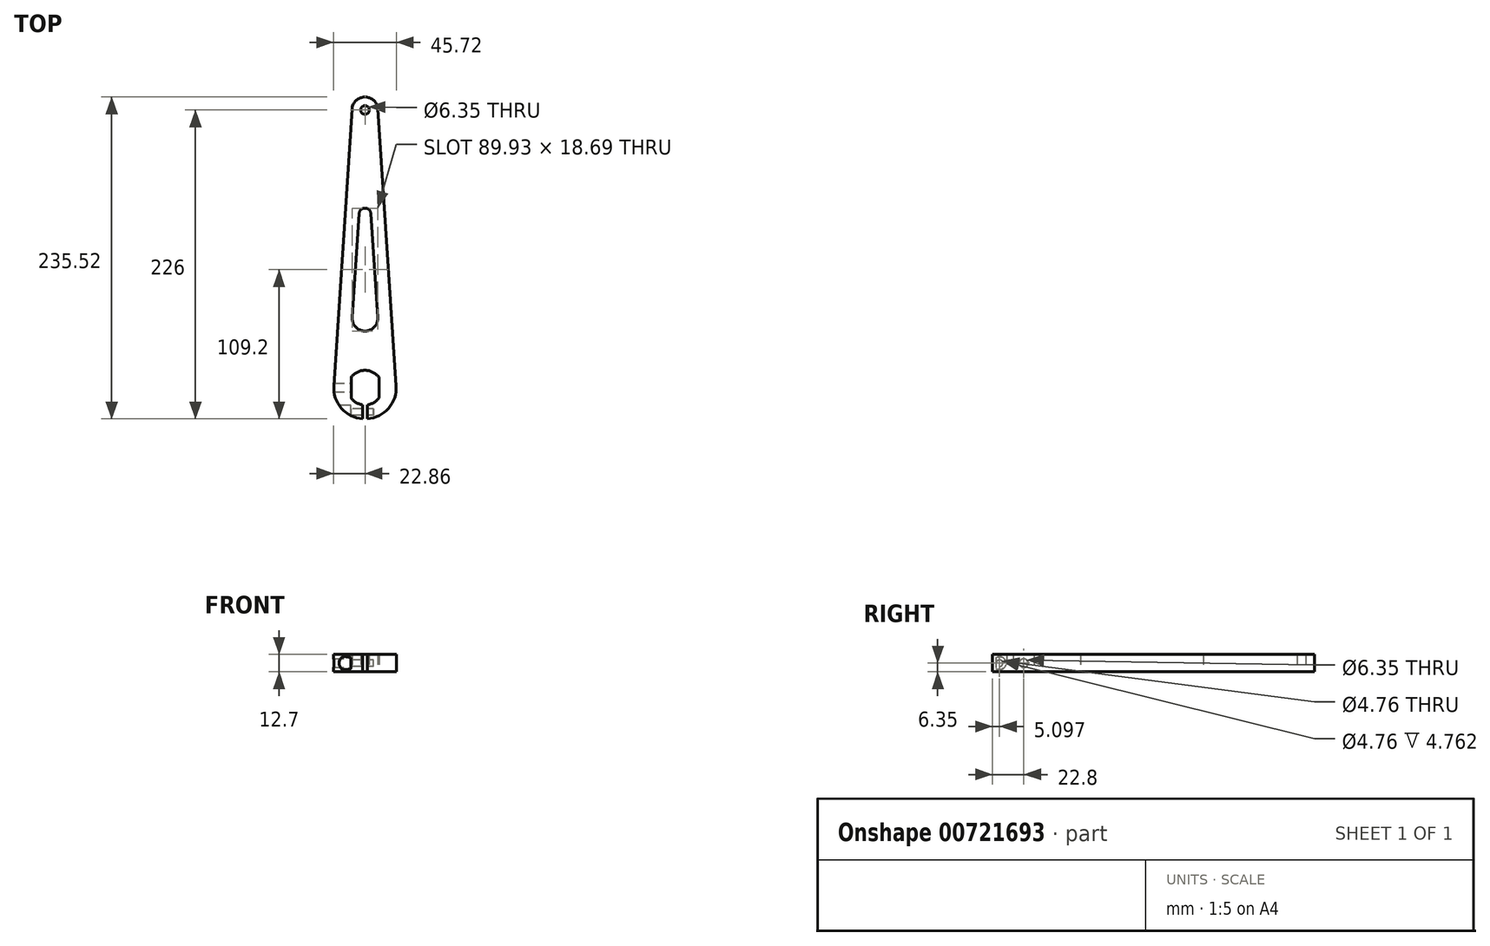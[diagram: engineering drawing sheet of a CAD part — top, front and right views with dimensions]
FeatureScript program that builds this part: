
annotation { "Feature Type Name" : "Feature", "Feature Type Description" : "" }
export const myFeature = defineFeature(function(context is Context, id is Id, definition is map)
    precondition{}
    {
        {
            var Q0;
            Q0=qCreatedBy(makeId("Top.planeOp"),FACE);
            var sketch = newSketch(context, id + "F0", { "sketchPlane" : qUnion([Q0])});
            skLineSegment(sketch, "E0", {"start": v(0, 220.9) * mm, "end": v(0, -303.4) * mm, "construction": true});
            skLineSegment(sketch, "E1", {"start": v(-22.81, 1.5) * mm, "end": v(-9.5, 203.83) * mm});
            skCircle(sketch, "E2", {"center": v(0, 203.2) * mm, "radius": 3.18 * mm});
            skArc(sketch, "E3.0", {"start": v(9.5, 203.83) * mm, "mid": v(0, 212.73) * mm, "end": v(-9.5, 203.83) * mm});
            skArc(sketch, "E4.0", {"start": v(-22.81, 1.5) * mm, "mid": v(-17.22, -15.04) * mm, "end": v(-1.59, -22.8) * mm});
            skLineSegment(sketch, "E5.MirrorCS", {"start": v(22.81, 1.5) * mm, "end": v(9.5, 203.83) * mm});
            skArc(sketch, "E6", {"start": v(-9.35, 51.41) * mm, "mid": v(0, 41.43) * mm, "end": v(9.35, 51.41) * mm});
            skLineSegment(sketch, "E7", {"start": v(9.35, 51.41) * mm, "end": v(4.36, 127.29) * mm});
            skArc(sketch, "E8", {"start": v(4.36, 127.29) * mm, "mid": v(0, 131.37) * mm, "end": v(-4.36, 127.29) * mm});
            skLineSegment(sketch, "E9.MirrorCS", {"start": v(-9.35, 51.41) * mm, "end": v(-4.36, 127.29) * mm});
            skArc(sketch, "E10", {"start": v(10.16, 7.62) * mm, "mid": v(0, 12.7) * mm, "end": v(-10.16, 7.62) * mm});
            skLineSegment(sketch, "E11", {"start": v(-10.16, 7.62) * mm, "end": v(-10.16, -7.62) * mm});
            skLineSegment(sketch, "E12.MirrorCS", {"start": v(10.16, 7.62) * mm, "end": v(10.16, -7.62) * mm});
            skArc(sketch, "E13.trimOffspring", {"start": v(-10.16, -7.62) * mm, "mid": v(-6.38, -10.98) * mm, "end": v(-1.59, -12.6) * mm});
            skLineSegment(sketch, "E14", {"start": v(-1.59, -12.6) * mm, "end": v(-1.59, -22.8) * mm});
            skLineSegment(sketch, "E15.MirrorCS", {"start": v(1.59, -12.6) * mm, "end": v(1.59, -22.8) * mm});
            skArc(sketch, "E16.trimOffspring", {"start": v(1.59, -12.6) * mm, "mid": v(6.38, -10.98) * mm, "end": v(10.16, -7.62) * mm});
            skArc(sketch, "E17.trimOffspring", {"start": v(1.59, -22.8) * mm, "mid": v(17.22, -15.04) * mm, "end": v(22.81, 1.5) * mm});
            skSolve(sketch);
        }
        {
            var Q0;
            Q0=qSketchRegion(id+"F0",true);
            extrude(context, id + "F1", {"entities" : qUnion([Q0]), "depth" : 12.7 * mm, "offsetDistance" : 25.4 * mm});
        }
        {
            var Q0;
            Q0=makeQuery(id+"F1.opExtrude","SWEPT_FACE",FACE,{"disambiguationData":[OSD([sQuery(id+"F0.wireOp",EDGE,"E11")])]});
            var sketch = newSketch(context, id + "F2", { "sketchPlane" : qUnion([Q0])});
            skCircle(sketch, "E18", {"center": v(0, 6.35) * mm, "radius": 3.18 * mm});
            skLineSegment(sketch, "E19", {"start": v(0, 0) * mm, "end": v(0, 12.7) * mm, "construction": true});
            skSolve(sketch);
        }
        {
            var Q0;
            Q0=qSketchRegion(id+"F2",true);
            extrude(context, id + "F3", {"entities" : qUnion([Q0]), "operationType" : NewBodyOperationType.REMOVE, "oppositeDirection" : true, "depth" : 25.4 * mm, "offsetDistance" : 25.4 * mm});
        }
        {
            var Q0;
            Q0=qCreatedBy(makeId("Right.planeOp"),FACE);
            var sketch = newSketch(context, id + "F4", { "sketchPlane" : qUnion([Q0])});
            skLineSegment(sketch, "E20", {"start": v(-22.8, 12.7) * mm, "end": v(-12.6, 12.7) * mm, "construction": true});
            skLineSegment(sketch, "E21", {"start": v(-17.7, 12.7) * mm, "end": v(-17.7, 0) * mm, "construction": true});
            skCircle(sketch, "E22", {"center": v(-17.7, 6.35) * mm, "radius": 2.38 * mm});
            skSolve(sketch);
        }
        {
            var Q0;
            Q0=qSketchRegion(id+"F4",true);
            var Q1;
            Q1=qConstructionFilter(qBodyType(qCreatedBy(id+"F4",EDGE),BodyType.WIRE),ConstructionObject.NO);
            extrude(context, id + "F5", {"entities" : qUnion([Q0]), "operationType" : NewBodyOperationType.REMOVE, "surfaceEntities" : qUnion([Q1]), "depth" : 6.35 * mm, "offsetDistance" : 25.4 * mm, "hasSecondDirection" : true, "secondDirectionBound" : SecondDirectionBoundingType.THROUGH_ALL, "secondDirectionOppositeDirection" : true, "secondDirectionDepth" : 25.4 * mm});
        }
        {
            var Q0;
            Q0=makeQuery(id+"F1.opExtrude","SWEPT_FACE",FACE,{"disambiguationData":[OSD([sQuery(id+"F0.wireOp",EDGE,"E14")])]});
            cPlane(context, id + "F6", {"entities" : qUnion([Q0]), "cplaneType" : CPlaneType.OFFSET, "offset" : 19.05 * mm, "oppositeDirection" : true, "width" : 152.4 * mm, "height" : 152.4 * mm});
        }
        {
            var Q0;
            Q0=qCreatedBy(id+"F6.planeOp",FACE);
            var sketch = newSketch(context, id + "F7", { "sketchPlane" : qUnion([Q0])});
            skCircle(sketch, "E23", {"center": v(-17.7, 6.35) * mm, "radius": 4.76 * mm});
            skSolve(sketch);
        }
        {
            var Q0;
            Q0=qSketchRegion(id+"F7",true);
            var Q1;
            Q1=qConstructionFilter(qBodyType(qCreatedBy(id+"F7",EDGE),BodyType.WIRE),ConstructionObject.NO);
            extrude(context, id + "F8", {"entities" : qUnion([Q0]), "operationType" : NewBodyOperationType.REMOVE, "surfaceEntities" : qUnion([Q1]), "depth" : 10.16 * mm, "offsetDistance" : 25.4 * mm});
        }
    });
